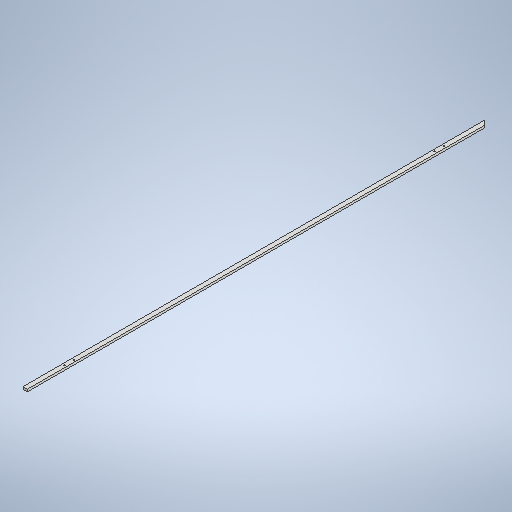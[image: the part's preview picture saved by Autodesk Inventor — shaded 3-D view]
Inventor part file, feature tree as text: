
AUTODESK INVENTOR PART (.ipt)
format: ipt  version: 2025.1 (Build 291241000, 241)  size: 282,112 bytes
history: native  units: mm
features: extrude x4, sketch x4, projected_geometry x1
ambient origin geometry x8: Origin, YZ Plane, XZ Plane, XY Plane, X Axis, Y Axis, Z Axis, Center Point
bodies: Solid1 (feature_tree)
feature tree (9):
  extrude  "Extrusion1"  Depth=2000.0mm
  extrude  "Extrusion2"  Depth=10.0mm TaperAngle=0.0deg
  extrude  "Extrusion3"  Depth=6.0mm
  extrude  "Extrusion4"  Depth=10.0mm
  sketch  "Sketch1"  dims[d0=19.0mm d1=2000.0mm]
  sketch  "Sketch2"  dims[d2=10.0mm d3=0.0mm d5=10.0mm d6=0.0mm]
  projected_geometry  "Projected Loop1"
  sketch  "Sketch3"  dims[d7=45.0deg d8=6.0mm]
  sketch  "Sketch4"  dims[d9=40.0mm d10=170.0mm d11=10.0mm d12=0.0mm d14=185.0mm d15=6.0mm d16=40.0mm d17=10.0mm d18=0.0mm]
